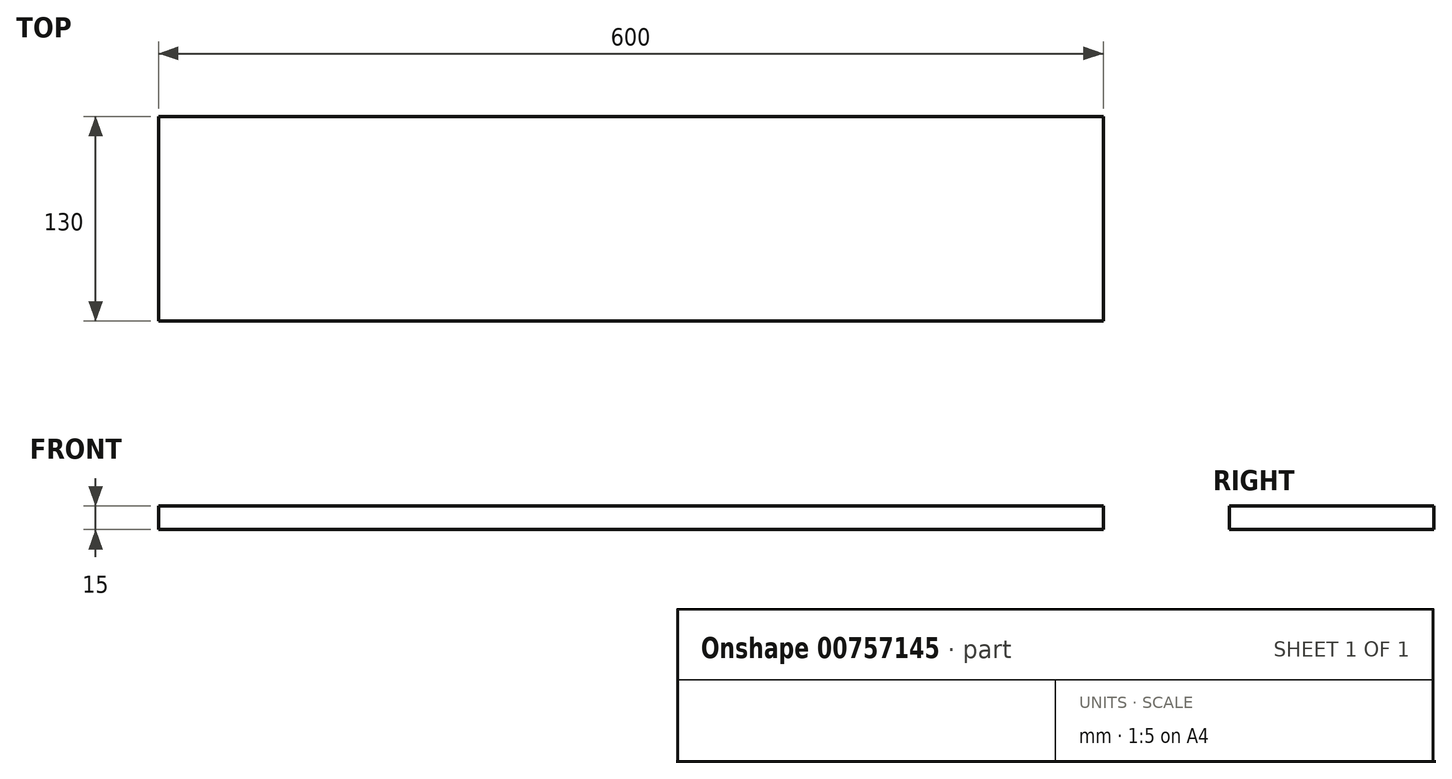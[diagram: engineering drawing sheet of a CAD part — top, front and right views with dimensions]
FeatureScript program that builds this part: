
annotation { "Feature Type Name" : "Feature", "Feature Type Description" : "" }
export const myFeature = defineFeature(function(context is Context, id is Id, definition is map)
    precondition{}
    {
        {
            var Q0;
            Q0=qCreatedBy(makeId("Right.planeOp"),FACE);
            var sketch = newSketch(context, id + "F0", { "sketchPlane" : qUnion([Q0])});
            skLineSegment(sketch, "E0.bottom", {"start": v(-65, 0) * mm, "end": v(65, 0) * mm});
            skLineSegment(sketch, "E0.top", {"start": v(-65, 15) * mm, "end": v(65, 15) * mm});
            skLineSegment(sketch, "E0.left", {"start": v(-65, 15) * mm, "end": v(-65, 0) * mm});
            skLineSegment(sketch, "E0.right", {"start": v(65, 15) * mm, "end": v(65, 0) * mm});
            skSolve(sketch);
        }
        {
            var Q0;
            Q0=makeQuery(id+"F0.imprint","IMPRINT",FACE,{"disambiguationData":[TD([[makeQuery(id+"F0.imprint","IMPRINT",EDGE,{"derivedFrom":sQuery(id+"F0.wireOp",EDGE,"E0.bottom")}),1.0]])]});
            extrude(context, id + "F1", {"entities" : qUnion([Q0]), "oppositeDirection" : true, "depth" : 300 * mm, "offsetDistance" : 25 * mm, "hasSecondDirection" : true, "secondDirectionOppositeDirection" : false, "secondDirectionDepth" : 300 * mm});
        }
    });
